# Revit family: Windows
name_source: partatom
category: Windows
revit_build: Autodesk Revit Architecture 2012 (Build: 20110309_2315(x64)
units: mm (PartAtom-declared; Revit-internal decimal feet)

## types (4) — shared parameters
Architrave = Yes
Architrave.Exterior = 80 mm  [stored 0.262467 ft]
Architrave.Interior = 40 mm  [stored 0.131234 ft]
Architrave.Width.Exterior = 150 mm
Architrave.Width.Interior = 80 mm  [stored 0.262467 ft]
Frame = <By Category>
Glass = <By Category>
Trim Exterior = <By Category>
Trim Interior = <By Category>
Wall Closure = By host
Window Inset = 30 mm  [stored 0.0984252 ft]

## per-type parameters (varying)
| type | Case_Height | Default Sill Height | Double window | Height | Rough Height | Rough Width | Single Window | Width |
| (0.90m x 1.80m) Single | 1500 mm  [stored 4.92126 ft] | 600 mm | No | 1800 mm  [stored 5.90551 ft] | 2400 mm | 900 mm  [stored 2.95276 ft] | Yes | 900 mm  [stored 2.95276 ft] |
| (1.80m x 1.80m) Double | 1500 mm  [stored 4.92126 ft] | 600 mm | Yes | 1800 mm  [stored 5.90551 ft] | 2400 mm | 1800 mm  [stored 5.90551 ft] | No | 1800 mm  [stored 5.90551 ft] |
| (0.90m x 0.60m) Bathroom | 400 mm  [stored 1.31234 ft] | 1500 mm  [stored 4.92126 ft] | No | 600 mm | 2100 mm | 900 mm  [stored 2.95276 ft] | No | 900 mm  [stored 2.95276 ft] |
| (1.80m x 1.50m) Kitchen | 1200 mm | 900 mm  [stored 2.95276 ft] | Yes | 1500 mm  [stored 4.92126 ft] | 2400 mm | 1800 mm  [stored 5.90551 ft] | No | 1800 mm  [stored 5.90551 ft] |

note: [stored X ft] marks values corroborated as IEEE doubles in the binary element streams (Revit-internal decimal feet)

## geometry (parser evidence)
native form markers: Sweep x1
no freeform markers — native parametric forms only
